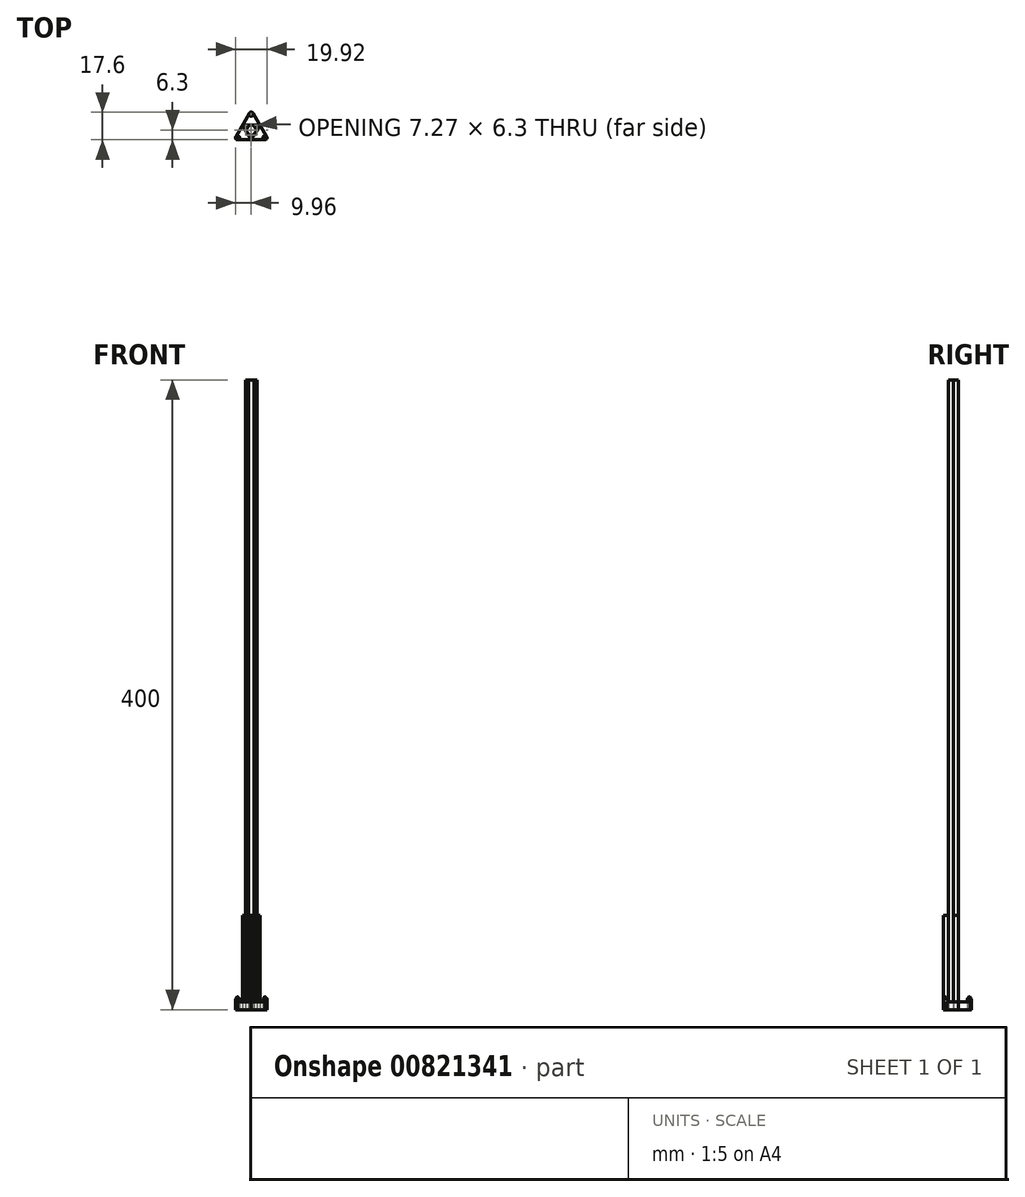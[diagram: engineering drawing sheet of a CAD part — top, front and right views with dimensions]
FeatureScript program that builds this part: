
annotation { "Feature Type Name" : "Feature", "Feature Type Description" : "" }
export const myFeature = defineFeature(function(context is Context, id is Id, definition is map)
    precondition{}
    {
        {
            var Q0;
            Q0=qCreatedBy(makeId("Top.planeOp"),FACE);
            var sketch = newSketch(context, id + "F0", { "sketchPlane" : qUnion([Q0])});
            skPoint(sketch, "E0.center", {"position": v(0, 0) * mm});
            skLineSegment(sketch, "E1", {"start": v(-10, 0) * mm, "end": v(10, 0) * mm});
            skCircle(sketch, "E2.cCircle", {"center": v(0, 0) * mm, "radius": 12.6 * mm, "construction": true});
            skLineSegment(sketch, "E2.0", {"start": v(0, 12.6) * mm, "end": v(10.91, -6.3) * mm});
            skLineSegment(sketch, "E2.1", {"start": v(10.91, -6.3) * mm, "end": v(-10.91, -6.3) * mm});
            skLineSegment(sketch, "E2.2", {"start": v(-10.91, -6.3) * mm, "end": v(0, 12.6) * mm});
            skCircle(sketch, "E3", {"center": v(0, 0) * mm, "radius": 10 * mm});
            skLineSegment(sketch, "E4", {"start": v(0, 0) * mm, "end": v(0, 12.6) * mm});
            skLineSegment(sketch, "E5", {"start": v(-10.91, -6.3) * mm, "end": v(0, 0) * mm});
            skLineSegment(sketch, "E6", {"start": v(0, 0) * mm, "end": v(10.91, -6.3) * mm});
            skCircle(sketch, "E7.cCircle", {"center": v(0, 0) * mm, "radius": 6.3 * mm, "construction": true});
            skLineSegment(sketch, "E7.0", {"start": v(5.46, 3.15) * mm, "end": v(0, -6.3) * mm});
            skLineSegment(sketch, "E7.1", {"start": v(0, -6.3) * mm, "end": v(-5.46, 3.15) * mm});
            skLineSegment(sketch, "E7.2", {"start": v(-5.46, 3.15) * mm, "end": v(5.46, 3.15) * mm});
            skCircle(sketch, "E8.cCircle", {"center": v(0, 0) * mm, "radius": 3.15 * mm, "construction": true});
            skLineSegment(sketch, "E8.0", {"start": v(2.73, -1.58) * mm, "end": v(-2.73, -1.58) * mm});
            skLineSegment(sketch, "E8.1", {"start": v(-2.73, -1.58) * mm, "end": v(0, 3.15) * mm});
            skLineSegment(sketch, "E8.2", {"start": v(0, 3.15) * mm, "end": v(2.73, -1.58) * mm});
            skCircle(sketch, "E9", {"center": v(0, 10) * mm, "radius": 1.3 * mm});
            skCircle(sketch, "E10", {"center": v(8.66, -5) * mm, "radius": 1.3 * mm});
            skCircle(sketch, "E11", {"center": v(-8.66, -5) * mm, "radius": 1.3 * mm});
            skLineSegment(sketch, "E12.0", {"start": v(0, 6.3) * mm, "end": v(5.46, -3.15) * mm});
            skLineSegment(sketch, "E12.1", {"start": v(5.46, -3.15) * mm, "end": v(-5.46, -3.15) * mm});
            skLineSegment(sketch, "E12.2", {"start": v(-5.46, -3.15) * mm, "end": v(0, 6.3) * mm});
            skSolve(sketch);
        }
        {
            var Q0;
            {var subQ6=sQuery(id+"F0.wireOp",EDGE,"E2.2");var subQ8=sQuery(id+"F0.wireOp",EDGE,"E3");var subQ9=makeQuery(id+"F0.imprint","INTERSECT",VERTEX,{"disambiguationData":[OD(1.0)],"derivedFrom":[subQ6,subQ8]});Q0=makeQuery(id+"F0.imprint","IMPRINT",FACE,{"disambiguationData":[TD([[makeQuery(id+"F0.imprint","IMPRINT",EDGE,{"disambiguationData":[TD([[subQ9,1.0]])],"derivedFrom":subQ8}),1.0]])]});}
            var Q1;
            {var subQ1=sQuery(id+"F0.wireOp",EDGE,"E2.0");var subQ9=sQuery(id+"F0.wireOp",EDGE,"E3");var subQ10=makeQuery(id+"F0.imprint","INTERSECT",VERTEX,{"disambiguationData":[OD(0.0)],"derivedFrom":[subQ1,subQ9]});Q1=makeQuery(id+"F0.imprint","IMPRINT",FACE,{"disambiguationData":[TD([[makeQuery(id+"F0.imprint","IMPRINT",EDGE,{"disambiguationData":[TD([[subQ10,-1.0]])],"derivedFrom":subQ9}),1.0]])]});}
            var Q2;
            {var subQ0=sQuery(id+"F0.wireOp",EDGE,"E2.2");var subQ1=sQuery(id+"F0.wireOp",EDGE,"E1");var subQ2=makeQuery(id+"F0.imprint","INTERSECT",VERTEX,{"derivedFrom":[subQ1,subQ0]});Q2=makeQuery(id+"F0.imprint","IMPRINT",FACE,{"disambiguationData":[TD([[makeQuery(id+"F0.imprint","IMPRINT",EDGE,{"disambiguationData":[TD([[subQ2,-1.0]])],"derivedFrom":subQ1}),1.0]])]});}
            var Q3;
            {var subQ5=sQuery(id+"F0.wireOp",EDGE,"E3");var subQ6=sQuery(id+"F0.wireOp",EDGE,"E2.2");var subQ7=makeQuery(id+"F0.imprint","INTERSECT",VERTEX,{"disambiguationData":[OD(0.0)],"derivedFrom":[subQ6,subQ5]});Q3=makeQuery(id+"F0.imprint","IMPRINT",FACE,{"disambiguationData":[TD([[makeQuery(id+"F0.imprint","IMPRINT",EDGE,{"disambiguationData":[TD([[subQ7,-1.0]])],"derivedFrom":subQ6}),-1.0]])]});}
            var Q4;
            {var subQ6=sQuery(id+"F0.wireOp",EDGE,"E2.1");var subQ9=sQuery(id+"F0.wireOp",EDGE,"E3");var subQ10=makeQuery(id+"F0.imprint","INTERSECT",VERTEX,{"disambiguationData":[OD(1.0)],"derivedFrom":[subQ6,subQ9]});Q4=makeQuery(id+"F0.imprint","IMPRINT",FACE,{"disambiguationData":[TD([[makeQuery(id+"F0.imprint","IMPRINT",EDGE,{"disambiguationData":[TD([[subQ10,1.0]])],"derivedFrom":subQ9}),1.0]])]});}
            var Q5;
            {var subQ1=sQuery(id+"F0.wireOp",EDGE,"E2.1");var subQ6=sQuery(id+"F0.wireOp",EDGE,"E3");var subQ11=makeQuery(id+"F0.imprint","INTERSECT",VERTEX,{"disambiguationData":[OD(0.0)],"derivedFrom":[subQ1,subQ6]});Q5=makeQuery(id+"F0.imprint","IMPRINT",FACE,{"disambiguationData":[TD([[makeQuery(id+"F0.imprint","IMPRINT",EDGE,{"disambiguationData":[TD([[subQ11,-1.0]])],"derivedFrom":subQ6}),1.0]])]});}
            var Q6;
            {var subQ5=sQuery(id+"F0.wireOp",EDGE,"E3");var subQ6=sQuery(id+"F0.wireOp",EDGE,"E2.0");var subQ7=makeQuery(id+"F0.imprint","INTERSECT",VERTEX,{"disambiguationData":[OD(1.0)],"derivedFrom":[subQ6,subQ5]});Q6=makeQuery(id+"F0.imprint","IMPRINT",FACE,{"disambiguationData":[TD([[makeQuery(id+"F0.imprint","IMPRINT",EDGE,{"disambiguationData":[TD([[subQ7,1.0]])],"derivedFrom":subQ6}),-1.0]])]});}
            var Q7;
            {var subQ0=sQuery(id+"F0.wireOp",EDGE,"E2.0");var subQ1=sQuery(id+"F0.wireOp",EDGE,"E1");var subQ2=makeQuery(id+"F0.imprint","INTERSECT",VERTEX,{"derivedFrom":[subQ1,subQ0]});Q7=makeQuery(id+"F0.imprint","IMPRINT",FACE,{"disambiguationData":[TD([[makeQuery(id+"F0.imprint","IMPRINT",EDGE,{"disambiguationData":[TD([[subQ2,1.0]])],"derivedFrom":subQ1}),1.0]])]});}
            var Q8;
            {var subQ0=sQuery(id+"F0.wireOp",EDGE,"E7.2");var subQ3=sQuery(id+"F0.wireOp",EDGE,"E12.2");var subQ5=makeQuery(id+"F0.imprint","INTERSECT",VERTEX,{"derivedFrom":[subQ0,subQ3]});Q8=makeQuery(id+"F0.imprint","IMPRINT",FACE,{"disambiguationData":[TD([[makeQuery(id+"F0.imprint","IMPRINT",EDGE,{"disambiguationData":[TD([[subQ5,1.0]])],"derivedFrom":subQ0}),-1.0]])]});}
            var Q9;
            {var subQ1=sQuery(id+"F0.wireOp",EDGE,"E7.0");var subQ3=sQuery(id+"F0.wireOp",EDGE,"E12.1");var subQ4=makeQuery(id+"F0.imprint","INTERSECT",VERTEX,{"derivedFrom":[subQ1,subQ3]});Q9=makeQuery(id+"F0.imprint","IMPRINT",FACE,{"disambiguationData":[TD([[makeQuery(id+"F0.imprint","IMPRINT",EDGE,{"disambiguationData":[TD([[subQ4,-1.0]])],"derivedFrom":subQ3}),1.0]])]});}
            var Q10;
            {var subQ0=sQuery(id+"F0.wireOp",EDGE,"E7.2");var subQ3=sQuery(id+"F0.wireOp",EDGE,"E12.0");var subQ5=makeQuery(id+"F0.imprint","INTERSECT",VERTEX,{"derivedFrom":[subQ0,subQ3]});Q10=makeQuery(id+"F0.imprint","IMPRINT",FACE,{"disambiguationData":[TD([[makeQuery(id+"F0.imprint","IMPRINT",EDGE,{"disambiguationData":[TD([[subQ5,-1.0]])],"derivedFrom":subQ0}),-1.0]])]});}
            var Q11;
            {var subQ0=sQuery(id+"F0.wireOp",EDGE,"E9");var subQ1=sQuery(id+"F0.wireOp",EDGE,"E2.0");var subQ2=makeQuery(id+"F0.imprint","INTERSECT",VERTEX,{"derivedFrom":[subQ1,subQ0]});Q11=makeQuery(id+"F0.imprint","IMPRINT",FACE,{"disambiguationData":[TD([[makeQuery(id+"F0.imprint","IMPRINT",EDGE,{"disambiguationData":[TD([[subQ2,-1.0]])],"derivedFrom":subQ1}),-1.0]])]});}
            var Q12;
            {var subQ0=sQuery(id+"F0.wireOp",EDGE,"E3");var subQ1=sQuery(id+"F0.wireOp",EDGE,"E2.2");var subQ2=makeQuery(id+"F0.imprint","INTERSECT",VERTEX,{"disambiguationData":[OD(1.0)],"derivedFrom":[subQ1,subQ0]});Q12=makeQuery(id+"F0.imprint","IMPRINT",FACE,{"disambiguationData":[TD([[makeQuery(id+"F0.imprint","IMPRINT",EDGE,{"disambiguationData":[TD([[subQ2,-1.0]])],"derivedFrom":subQ1}),-1.0]])]});}
            var Q13;
            {var subQ0=sQuery(id+"F0.wireOp",EDGE,"E11");var subQ1=sQuery(id+"F0.wireOp",EDGE,"E2.2");var subQ2=makeQuery(id+"F0.imprint","INTERSECT",VERTEX,{"derivedFrom":[subQ1,subQ0]});Q13=makeQuery(id+"F0.imprint","IMPRINT",FACE,{"disambiguationData":[TD([[makeQuery(id+"F0.imprint","IMPRINT",EDGE,{"disambiguationData":[TD([[subQ2,-1.0]])],"derivedFrom":subQ1}),-1.0]])]});}
            var Q14;
            {var subQ0=sQuery(id+"F0.wireOp",EDGE,"E3");var subQ1=sQuery(id+"F0.wireOp",EDGE,"E2.1");var subQ2=makeQuery(id+"F0.imprint","INTERSECT",VERTEX,{"disambiguationData":[OD(1.0)],"derivedFrom":[subQ1,subQ0]});Q14=makeQuery(id+"F0.imprint","IMPRINT",FACE,{"disambiguationData":[TD([[makeQuery(id+"F0.imprint","IMPRINT",EDGE,{"disambiguationData":[TD([[subQ2,-1.0]])],"derivedFrom":subQ1}),-1.0]])]});}
            var Q15;
            {var subQ0=sQuery(id+"F0.wireOp",EDGE,"E3");var subQ1=sQuery(id+"F0.wireOp",EDGE,"E2.0");var subQ2=makeQuery(id+"F0.imprint","INTERSECT",VERTEX,{"disambiguationData":[OD(1.0)],"derivedFrom":[subQ1,subQ0]});Q15=makeQuery(id+"F0.imprint","IMPRINT",FACE,{"disambiguationData":[TD([[makeQuery(id+"F0.imprint","IMPRINT",EDGE,{"disambiguationData":[TD([[subQ2,-1.0]])],"derivedFrom":subQ1}),-1.0]])]});}
            var Q16;
            {var subQ0=sQuery(id+"F0.wireOp",EDGE,"E10");var subQ1=sQuery(id+"F0.wireOp",EDGE,"E2.1");var subQ2=makeQuery(id+"F0.imprint","INTERSECT",VERTEX,{"derivedFrom":[subQ1,subQ0]});Q16=makeQuery(id+"F0.imprint","IMPRINT",FACE,{"disambiguationData":[TD([[makeQuery(id+"F0.imprint","IMPRINT",EDGE,{"disambiguationData":[TD([[subQ2,-1.0]])],"derivedFrom":subQ1}),-1.0]])]});}
            var Q17;
            {var subQ1=sQuery(id+"F0.wireOp",EDGE,"E6");var subQ3=sQuery(id+"F0.wireOp",EDGE,"E12.0");var subQ4=makeQuery(id+"F0.imprint","INTERSECT",VERTEX,{"derivedFrom":[subQ1,subQ3,sQuery(id+"F0.wireOp",EDGE,"E12.1")]});Q17=makeQuery(id+"F0.imprint","IMPRINT",FACE,{"disambiguationData":[TD([[makeQuery(id+"F0.imprint","IMPRINT",EDGE,{"disambiguationData":[TD([[subQ4,1.0]])],"derivedFrom":subQ3}),-1.0]])]});}
            var Q18;
            {var subQ0=sQuery(id+"F0.wireOp",EDGE,"E7.0");var subQ3=sQuery(id+"F0.wireOp",EDGE,"E12.1");var subQ5=makeQuery(id+"F0.imprint","INTERSECT",VERTEX,{"derivedFrom":[subQ0,subQ3]});Q18=makeQuery(id+"F0.imprint","IMPRINT",FACE,{"disambiguationData":[TD([[makeQuery(id+"F0.imprint","IMPRINT",EDGE,{"disambiguationData":[TD([[subQ5,1.0]])],"derivedFrom":subQ3}),-1.0]])]});}
            var Q19;
            {var subQ1=sQuery(id+"F0.wireOp",EDGE,"E5");var subQ3=sQuery(id+"F0.wireOp",EDGE,"E12.2");var subQ4=makeQuery(id+"F0.imprint","INTERSECT",VERTEX,{"derivedFrom":[subQ1,sQuery(id+"F0.wireOp",EDGE,"E12.1"),subQ3]});Q19=makeQuery(id+"F0.imprint","IMPRINT",FACE,{"disambiguationData":[TD([[makeQuery(id+"F0.imprint","IMPRINT",EDGE,{"disambiguationData":[TD([[subQ4,-1.0]])],"derivedFrom":subQ3}),-1.0]])]});}
            var Q20;
            {var subQ0=sQuery(id+"F0.wireOp",EDGE,"E7.1");var subQ3=sQuery(id+"F0.wireOp",EDGE,"E12.1");var subQ5=makeQuery(id+"F0.imprint","INTERSECT",VERTEX,{"derivedFrom":[subQ0,subQ3]});Q20=makeQuery(id+"F0.imprint","IMPRINT",FACE,{"disambiguationData":[TD([[makeQuery(id+"F0.imprint","IMPRINT",EDGE,{"disambiguationData":[TD([[subQ5,-1.0]])],"derivedFrom":subQ3}),-1.0]])]});}
            var Q21;
            {var subQ0=sQuery(id+"F0.wireOp",EDGE,"E7.2");var subQ3=sQuery(id+"F0.wireOp",EDGE,"E12.2");var subQ5=makeQuery(id+"F0.imprint","INTERSECT",VERTEX,{"derivedFrom":[subQ0,subQ3]});Q21=makeQuery(id+"F0.imprint","IMPRINT",FACE,{"disambiguationData":[TD([[makeQuery(id+"F0.imprint","IMPRINT",EDGE,{"disambiguationData":[TD([[subQ5,-1.0]])],"derivedFrom":subQ3}),-1.0]])]});}
            var Q22;
            {var subQ0=sQuery(id+"F0.wireOp",EDGE,"E7.2");var subQ3=sQuery(id+"F0.wireOp",EDGE,"E12.0");var subQ5=makeQuery(id+"F0.imprint","INTERSECT",VERTEX,{"derivedFrom":[subQ0,subQ3]});Q22=makeQuery(id+"F0.imprint","IMPRINT",FACE,{"disambiguationData":[TD([[makeQuery(id+"F0.imprint","IMPRINT",EDGE,{"disambiguationData":[TD([[subQ5,1.0]])],"derivedFrom":subQ3}),-1.0]])]});}
            extrude(context, id + "F1", {"entities" : qUnion([Q0, Q1, Q2, Q3, Q4, Q5, Q6, Q7, Q8, Q9, Q10, Q11, Q12, Q13, Q14, Q15, Q16, Q17, Q18, Q19, Q20, Q21, Q22]), "depth" : 5 * mm, "offsetDistance" : 25 * mm});
        }
        {
            var Q0;
            {var subQ0=sQuery(id+"F0.wireOp",EDGE,"E7.2");var subQ3=sQuery(id+"F0.wireOp",EDGE,"E12.2");var subQ5=makeQuery(id+"F0.imprint","INTERSECT",VERTEX,{"derivedFrom":[subQ0,subQ3]});Q0=makeQuery(id+"F0.imprint","IMPRINT",FACE,{"disambiguationData":[TD([[makeQuery(id+"F0.imprint","IMPRINT",EDGE,{"disambiguationData":[TD([[subQ5,1.0]])],"derivedFrom":subQ0}),-1.0]])]});}
            var Q1;
            {var subQ1=sQuery(id+"F0.wireOp",EDGE,"E7.0");var subQ3=sQuery(id+"F0.wireOp",EDGE,"E12.1");var subQ4=makeQuery(id+"F0.imprint","INTERSECT",VERTEX,{"derivedFrom":[subQ1,subQ3]});Q1=makeQuery(id+"F0.imprint","IMPRINT",FACE,{"disambiguationData":[TD([[makeQuery(id+"F0.imprint","IMPRINT",EDGE,{"disambiguationData":[TD([[subQ4,-1.0]])],"derivedFrom":subQ3}),1.0]])]});}
            var Q2;
            {var subQ0=sQuery(id+"F0.wireOp",EDGE,"E7.2");var subQ3=sQuery(id+"F0.wireOp",EDGE,"E12.0");var subQ5=makeQuery(id+"F0.imprint","INTERSECT",VERTEX,{"derivedFrom":[subQ0,subQ3]});Q2=makeQuery(id+"F0.imprint","IMPRINT",FACE,{"disambiguationData":[TD([[makeQuery(id+"F0.imprint","IMPRINT",EDGE,{"disambiguationData":[TD([[subQ5,-1.0]])],"derivedFrom":subQ0}),-1.0]])]});}
            extrude(context, id + "F2", {"entities" : qUnion([Q0, Q1, Q2]), "depth" : 60 * mm, "offsetDistance" : 25 * mm});
        }
        {
            var Q0;
            {var subQ0=sQuery(id+"F0.wireOp",EDGE,"E8.2");var subQ1=sQuery(id+"F0.wireOp",EDGE,"E1");var subQ2=makeQuery(id+"F0.imprint","INTERSECT",VERTEX,{"derivedFrom":[subQ1,subQ0]});Q0=makeQuery(id+"F0.imprint","IMPRINT",FACE,{"disambiguationData":[TD([[makeQuery(id+"F0.imprint","IMPRINT",EDGE,{"disambiguationData":[TD([[subQ2,-1.0]])],"derivedFrom":subQ1}),1.0]])]});}
            var Q1;
            {var subQ0=sQuery(id+"F0.wireOp",EDGE,"E8.1");var subQ1=sQuery(id+"F0.wireOp",EDGE,"E1");var subQ2=makeQuery(id+"F0.imprint","INTERSECT",VERTEX,{"derivedFrom":[subQ1,subQ0]});Q1=makeQuery(id+"F0.imprint","IMPRINT",FACE,{"disambiguationData":[TD([[makeQuery(id+"F0.imprint","IMPRINT",EDGE,{"disambiguationData":[TD([[subQ2,1.0]])],"derivedFrom":subQ1}),1.0]])]});}
            var Q2;
            {var subQ0=sQuery(id+"F0.wireOp",EDGE,"E8.1");var subQ1=sQuery(id+"F0.wireOp",EDGE,"E1");var subQ2=makeQuery(id+"F0.imprint","INTERSECT",VERTEX,{"derivedFrom":[subQ1,subQ0]});Q2=makeQuery(id+"F0.imprint","IMPRINT",FACE,{"disambiguationData":[TD([[makeQuery(id+"F0.imprint","IMPRINT",EDGE,{"disambiguationData":[TD([[subQ2,1.0]])],"derivedFrom":subQ1}),-1.0]])]});}
            var Q3;
            {var subQ0=sQuery(id+"F0.wireOp",EDGE,"E8.0");Q3=makeQuery(id+"F0.imprint","IMPRINT",FACE,{"disambiguationData":[TD([[makeQuery(id+"F0.imprint","IMPRINT",EDGE,{"derivedFrom":subQ0}),1.0]])]});}
            var Q4;
            {var subQ0=sQuery(id+"F0.wireOp",EDGE,"E8.2");var subQ1=sQuery(id+"F0.wireOp",EDGE,"E1");var subQ2=makeQuery(id+"F0.imprint","INTERSECT",VERTEX,{"derivedFrom":[subQ1,subQ0]});Q4=makeQuery(id+"F0.imprint","IMPRINT",FACE,{"disambiguationData":[TD([[makeQuery(id+"F0.imprint","IMPRINT",EDGE,{"disambiguationData":[TD([[subQ2,-1.0]])],"derivedFrom":subQ1}),-1.0]])]});}
            var Q5;
            {var subQ1=sQuery(id+"F0.wireOp",EDGE,"E1");var subQ3=sQuery(id+"F0.wireOp",EDGE,"E8.2");var subQ4=makeQuery(id+"F0.imprint","INTERSECT",VERTEX,{"derivedFrom":[subQ1,subQ3]});Q5=makeQuery(id+"F0.imprint","IMPRINT",FACE,{"disambiguationData":[TD([[makeQuery(id+"F0.imprint","IMPRINT",EDGE,{"disambiguationData":[TD([[subQ4,1.0]])],"derivedFrom":subQ1}),-1.0]])]});}
            var Q6;
            {var subQ3=sQuery(id+"F0.wireOp",EDGE,"E8.0");Q6=makeQuery(id+"F0.imprint","IMPRINT",FACE,{"disambiguationData":[TD([[makeQuery(id+"F0.imprint","IMPRINT",EDGE,{"derivedFrom":subQ3}),-1.0]])]});}
            var Q7;
            {var subQ1=sQuery(id+"F0.wireOp",EDGE,"E1");var subQ3=sQuery(id+"F0.wireOp",EDGE,"E8.1");var subQ4=makeQuery(id+"F0.imprint","INTERSECT",VERTEX,{"derivedFrom":[subQ1,subQ3]});Q7=makeQuery(id+"F0.imprint","IMPRINT",FACE,{"disambiguationData":[TD([[makeQuery(id+"F0.imprint","IMPRINT",EDGE,{"disambiguationData":[TD([[subQ4,-1.0]])],"derivedFrom":subQ1}),-1.0]])]});}
            var Q8;
            {var subQ1=sQuery(id+"F0.wireOp",EDGE,"E1");var subQ3=sQuery(id+"F0.wireOp",EDGE,"E8.1");var subQ4=makeQuery(id+"F0.imprint","INTERSECT",VERTEX,{"derivedFrom":[subQ1,subQ3]});Q8=makeQuery(id+"F0.imprint","IMPRINT",FACE,{"disambiguationData":[TD([[makeQuery(id+"F0.imprint","IMPRINT",EDGE,{"disambiguationData":[TD([[subQ4,-1.0]])],"derivedFrom":subQ1}),1.0]])]});}
            var Q9;
            {var subQ0=sQuery(id+"F0.wireOp",EDGE,"E8.0");Q9=makeQuery(id+"F0.imprint","IMPRINT",FACE,{"disambiguationData":[TD([[makeQuery(id+"F0.imprint","IMPRINT",EDGE,{"derivedFrom":subQ0}),1.0]])]});}
            var Q10;
            {var subQ3=sQuery(id+"F0.wireOp",EDGE,"E8.0");Q10=makeQuery(id+"F0.imprint","IMPRINT",FACE,{"disambiguationData":[TD([[makeQuery(id+"F0.imprint","IMPRINT",EDGE,{"derivedFrom":subQ3}),-1.0]])]});}
            var Q11;
            {var subQ1=sQuery(id+"F0.wireOp",EDGE,"E1");var subQ3=sQuery(id+"F0.wireOp",EDGE,"E8.1");var subQ4=makeQuery(id+"F0.imprint","INTERSECT",VERTEX,{"derivedFrom":[subQ1,subQ3]});Q11=makeQuery(id+"F0.imprint","IMPRINT",FACE,{"disambiguationData":[TD([[makeQuery(id+"F0.imprint","IMPRINT",EDGE,{"disambiguationData":[TD([[subQ4,-1.0]])],"derivedFrom":subQ1}),-1.0]])]});}
            var Q12;
            {var subQ0=sQuery(id+"F0.wireOp",EDGE,"E8.1");var subQ1=sQuery(id+"F0.wireOp",EDGE,"E1");var subQ2=makeQuery(id+"F0.imprint","INTERSECT",VERTEX,{"derivedFrom":[subQ1,subQ0]});Q12=makeQuery(id+"F0.imprint","IMPRINT",FACE,{"disambiguationData":[TD([[makeQuery(id+"F0.imprint","IMPRINT",EDGE,{"disambiguationData":[TD([[subQ2,1.0]])],"derivedFrom":subQ1}),-1.0]])]});}
            var Q13;
            {var subQ0=sQuery(id+"F0.wireOp",EDGE,"E8.1");var subQ1=sQuery(id+"F0.wireOp",EDGE,"E1");var subQ2=makeQuery(id+"F0.imprint","INTERSECT",VERTEX,{"derivedFrom":[subQ1,subQ0]});Q13=makeQuery(id+"F0.imprint","IMPRINT",FACE,{"disambiguationData":[TD([[makeQuery(id+"F0.imprint","IMPRINT",EDGE,{"disambiguationData":[TD([[subQ2,1.0]])],"derivedFrom":subQ1}),1.0]])]});}
            var Q14;
            {var subQ0=sQuery(id+"F0.wireOp",EDGE,"E8.2");var subQ1=sQuery(id+"F0.wireOp",EDGE,"E1");var subQ2=makeQuery(id+"F0.imprint","INTERSECT",VERTEX,{"derivedFrom":[subQ1,subQ0]});Q14=makeQuery(id+"F0.imprint","IMPRINT",FACE,{"disambiguationData":[TD([[makeQuery(id+"F0.imprint","IMPRINT",EDGE,{"disambiguationData":[TD([[subQ2,-1.0]])],"derivedFrom":subQ1}),1.0]])]});}
            var Q15;
            {var subQ0=sQuery(id+"F0.wireOp",EDGE,"E8.2");var subQ1=sQuery(id+"F0.wireOp",EDGE,"E1");var subQ2=makeQuery(id+"F0.imprint","INTERSECT",VERTEX,{"derivedFrom":[subQ1,subQ0]});Q15=makeQuery(id+"F0.imprint","IMPRINT",FACE,{"disambiguationData":[TD([[makeQuery(id+"F0.imprint","IMPRINT",EDGE,{"disambiguationData":[TD([[subQ2,-1.0]])],"derivedFrom":subQ1}),-1.0]])]});}
            var Q16;
            {var subQ1=sQuery(id+"F0.wireOp",EDGE,"E1");var subQ3=sQuery(id+"F0.wireOp",EDGE,"E8.1");var subQ4=makeQuery(id+"F0.imprint","INTERSECT",VERTEX,{"derivedFrom":[subQ1,subQ3]});Q16=makeQuery(id+"F0.imprint","IMPRINT",FACE,{"disambiguationData":[TD([[makeQuery(id+"F0.imprint","IMPRINT",EDGE,{"disambiguationData":[TD([[subQ4,-1.0]])],"derivedFrom":subQ1}),1.0]])]});}
            var Q17;
            {var subQ1=sQuery(id+"F0.wireOp",EDGE,"E1");var subQ3=sQuery(id+"F0.wireOp",EDGE,"E8.2");var subQ4=makeQuery(id+"F0.imprint","INTERSECT",VERTEX,{"derivedFrom":[subQ1,subQ3]});Q17=makeQuery(id+"F0.imprint","IMPRINT",FACE,{"disambiguationData":[TD([[makeQuery(id+"F0.imprint","IMPRINT",EDGE,{"disambiguationData":[TD([[subQ4,1.0]])],"derivedFrom":subQ1}),1.0]])]});}
            extrude(context, id + "F3", {"entities" : qUnion([Q0, Q1, Q2, Q3, Q4, Q5, Q6, Q7, Q8, Q9, Q10, Q11, Q12, Q13, Q14, Q15, Q16, Q17]), "depth" : 400 * mm, "offsetDistance" : 25 * mm});
        }
        {
            var Q0;
            {var subQ0=sQuery(id+"F0.wireOp",EDGE,"E4");var subQ1=sQuery(id+"F0.wireOp",EDGE,"E3");var subQ2=makeQuery(id+"F0.imprint","INTERSECT",VERTEX,{"derivedFrom":[subQ1,subQ0]});Q0=makeQuery(id+"F0.imprint","IMPRINT",FACE,{"disambiguationData":[TD([[makeQuery(id+"F0.imprint","IMPRINT",EDGE,{"disambiguationData":[TD([[subQ2,-1.0]])],"derivedFrom":subQ1}),-1.0]])]});}
            var Q1;
            {var subQ0=sQuery(id+"F0.wireOp",EDGE,"E4");var subQ1=sQuery(id+"F0.wireOp",EDGE,"E3");var subQ2=makeQuery(id+"F0.imprint","INTERSECT",VERTEX,{"derivedFrom":[subQ1,subQ0]});Q1=makeQuery(id+"F0.imprint","IMPRINT",FACE,{"disambiguationData":[TD([[makeQuery(id+"F0.imprint","IMPRINT",EDGE,{"disambiguationData":[TD([[subQ2,-1.0]])],"derivedFrom":subQ1}),1.0]])]});}
            var Q2;
            {var subQ0=sQuery(id+"F0.wireOp",EDGE,"E9");var subQ1=sQuery(id+"F0.wireOp",EDGE,"E3");var subQ2=makeQuery(id+"F0.imprint","INTERSECT",VERTEX,{"disambiguationData":[OD(0.0)],"derivedFrom":[subQ1,subQ0]});Q2=makeQuery(id+"F0.imprint","IMPRINT",FACE,{"disambiguationData":[TD([[makeQuery(id+"F0.imprint","IMPRINT",EDGE,{"disambiguationData":[TD([[subQ2,-1.0]])],"derivedFrom":subQ1}),1.0]])]});}
            var Q3;
            {var subQ0=sQuery(id+"F0.wireOp",EDGE,"E9");var subQ1=sQuery(id+"F0.wireOp",EDGE,"E3");var subQ2=makeQuery(id+"F0.imprint","INTERSECT",VERTEX,{"disambiguationData":[OD(0.0)],"derivedFrom":[subQ1,subQ0]});Q3=makeQuery(id+"F0.imprint","IMPRINT",FACE,{"disambiguationData":[TD([[makeQuery(id+"F0.imprint","IMPRINT",EDGE,{"disambiguationData":[TD([[subQ2,-1.0]])],"derivedFrom":subQ1}),-1.0]])]});}
            var Q4;
            {var subQ0=sQuery(id+"F0.wireOp",EDGE,"E11");var subQ1=sQuery(id+"F0.wireOp",EDGE,"E3");var subQ2=makeQuery(id+"F0.imprint","INTERSECT",VERTEX,{"disambiguationData":[OD(0.0)],"derivedFrom":[subQ1,subQ0]});Q4=makeQuery(id+"F0.imprint","IMPRINT",FACE,{"disambiguationData":[TD([[makeQuery(id+"F0.imprint","IMPRINT",EDGE,{"disambiguationData":[TD([[subQ2,-1.0]])],"derivedFrom":subQ1}),-1.0]])]});}
            var Q5;
            {var subQ0=sQuery(id+"F0.wireOp",EDGE,"E5");var subQ1=sQuery(id+"F0.wireOp",EDGE,"E3");var subQ2=makeQuery(id+"F0.imprint","INTERSECT",VERTEX,{"derivedFrom":[subQ1,subQ0]});Q5=makeQuery(id+"F0.imprint","IMPRINT",FACE,{"disambiguationData":[TD([[makeQuery(id+"F0.imprint","IMPRINT",EDGE,{"disambiguationData":[TD([[subQ2,-1.0]])],"derivedFrom":subQ1}),-1.0]])]});}
            var Q6;
            {var subQ0=sQuery(id+"F0.wireOp",EDGE,"E5");var subQ1=sQuery(id+"F0.wireOp",EDGE,"E3");var subQ2=makeQuery(id+"F0.imprint","INTERSECT",VERTEX,{"derivedFrom":[subQ1,subQ0]});Q6=makeQuery(id+"F0.imprint","IMPRINT",FACE,{"disambiguationData":[TD([[makeQuery(id+"F0.imprint","IMPRINT",EDGE,{"disambiguationData":[TD([[subQ2,-1.0]])],"derivedFrom":subQ1}),1.0]])]});}
            var Q7;
            {var subQ0=sQuery(id+"F0.wireOp",EDGE,"E11");var subQ1=sQuery(id+"F0.wireOp",EDGE,"E3");var subQ2=makeQuery(id+"F0.imprint","INTERSECT",VERTEX,{"disambiguationData":[OD(0.0)],"derivedFrom":[subQ1,subQ0]});Q7=makeQuery(id+"F0.imprint","IMPRINT",FACE,{"disambiguationData":[TD([[makeQuery(id+"F0.imprint","IMPRINT",EDGE,{"disambiguationData":[TD([[subQ2,-1.0]])],"derivedFrom":subQ1}),1.0]])]});}
            var Q8;
            {var subQ0=sQuery(id+"F0.wireOp",EDGE,"E10");var subQ1=sQuery(id+"F0.wireOp",EDGE,"E3");var subQ2=makeQuery(id+"F0.imprint","INTERSECT",VERTEX,{"disambiguationData":[OD(0.0)],"derivedFrom":[subQ1,subQ0]});Q8=makeQuery(id+"F0.imprint","IMPRINT",FACE,{"disambiguationData":[TD([[makeQuery(id+"F0.imprint","IMPRINT",EDGE,{"disambiguationData":[TD([[subQ2,-1.0]])],"derivedFrom":subQ1}),1.0]])]});}
            var Q9;
            {var subQ0=sQuery(id+"F0.wireOp",EDGE,"E6");var subQ1=sQuery(id+"F0.wireOp",EDGE,"E3");var subQ2=makeQuery(id+"F0.imprint","INTERSECT",VERTEX,{"derivedFrom":[subQ1,subQ0]});Q9=makeQuery(id+"F0.imprint","IMPRINT",FACE,{"disambiguationData":[TD([[makeQuery(id+"F0.imprint","IMPRINT",EDGE,{"disambiguationData":[TD([[subQ2,-1.0]])],"derivedFrom":subQ1}),1.0]])]});}
            var Q10;
            {var subQ0=sQuery(id+"F0.wireOp",EDGE,"E6");var subQ1=sQuery(id+"F0.wireOp",EDGE,"E3");var subQ2=makeQuery(id+"F0.imprint","INTERSECT",VERTEX,{"derivedFrom":[subQ1,subQ0]});Q10=makeQuery(id+"F0.imprint","IMPRINT",FACE,{"disambiguationData":[TD([[makeQuery(id+"F0.imprint","IMPRINT",EDGE,{"disambiguationData":[TD([[subQ2,-1.0]])],"derivedFrom":subQ1}),-1.0]])]});}
            var Q11;
            {var subQ0=sQuery(id+"F0.wireOp",EDGE,"E10");var subQ1=sQuery(id+"F0.wireOp",EDGE,"E3");var subQ2=makeQuery(id+"F0.imprint","INTERSECT",VERTEX,{"disambiguationData":[OD(0.0)],"derivedFrom":[subQ1,subQ0]});Q11=makeQuery(id+"F0.imprint","IMPRINT",FACE,{"disambiguationData":[TD([[makeQuery(id+"F0.imprint","IMPRINT",EDGE,{"disambiguationData":[TD([[subQ2,-1.0]])],"derivedFrom":subQ1}),-1.0]])]});}
            extrude(context, id + "F4", {"entities" : qUnion([Q0, Q1, Q2, Q3, Q4, Q5, Q6, Q7, Q8, Q9, Q10, Q11]), "depth" : 8 * mm, "offsetDistance" : 25 * mm});
        }
        {
            var Q0;
            Q0=makeQuery(id+"F4.opExtrude","CAP_EDGE",EDGE,{"disambiguationData":[OSD([sQuery(id+"F0.wireOp",EDGE,"E11")])],"isStart":false});
            var Q1;
            Q1=makeQuery(id+"F4.opExtrude","CAP_EDGE",EDGE,{"disambiguationData":[OSD([sQuery(id+"F0.wireOp",EDGE,"E10")])],"isStart":false});
            var Q2;
            Q2=makeQuery(id+"F4.opExtrude","CAP_EDGE",EDGE,{"disambiguationData":[OSD([sQuery(id+"F0.wireOp",EDGE,"E9")])],"isStart":false});
            chamfer(context, id + "F5", {"entities" : qUnion([Q0, Q1, Q2]), "width" : 1 * mm, "tangentPropagation" : true});
        }
    });
